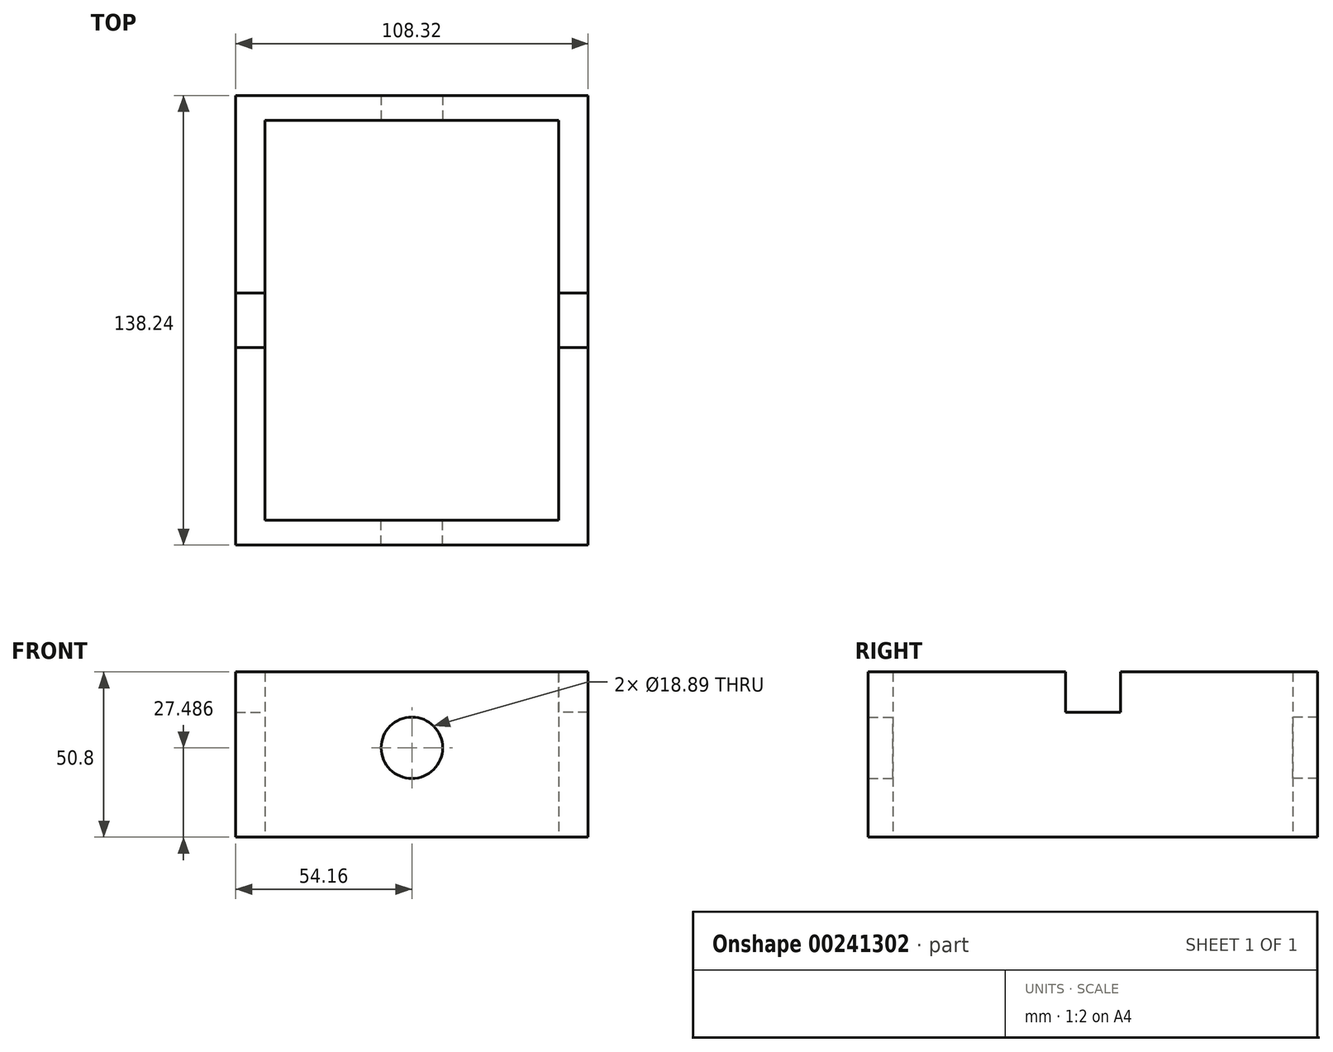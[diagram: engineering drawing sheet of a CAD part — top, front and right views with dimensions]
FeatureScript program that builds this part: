
annotation { "Feature Type Name" : "Feature", "Feature Type Description" : "" }
export const myFeature = defineFeature(function(context is Context, id is Id, definition is map)
    precondition{}
    {
        {
            var Q0;
            Q0=qCreatedBy(makeId("Top.planeOp"),FACE);
            var sketch = newSketch(context, id + "F0", { "sketchPlane" : qUnion([Q0])});
            skLineSegment(sketch, "E0.bottom", {"start": v(54.16, -69.12) * mm, "end": v(-54.16, -69.12) * mm});
            skLineSegment(sketch, "E0.top", {"start": v(54.16, 69.12) * mm, "end": v(-54.16, 69.12) * mm});
            skLineSegment(sketch, "E0.left", {"start": v(54.16, -69.12) * mm, "end": v(54.16, 69.12) * mm});
            skLineSegment(sketch, "E0.right", {"start": v(-54.16, -69.12) * mm, "end": v(-54.16, 69.12) * mm});
            skPoint(sketch, "E0.middle", {"position": v(0, 0) * mm});
            skSolve(sketch);
        }
        {
            var Q0;
            Q0=makeQuery(id+"F0.imprint","IMPRINT",FACE,{"disambiguationData":[TD([[makeQuery(id+"F0.imprint","IMPRINT",EDGE,{"derivedFrom":sQuery(id+"F0.wireOp",EDGE,"E0.bottom")}),-1.0]])]});
            extrude(context, id + "F1", {"entities" : qUnion([Q0]), "depth" : 50.8 * mm});
        }
        {
            var Q0;
            Q0=qCreatedBy(makeId("Top.planeOp"),FACE);
            var sketch = newSketch(context, id + "F2", { "sketchPlane" : qUnion([Q0])});
            skLineSegment(sketch, "E1.bottom", {"start": v(45.18, -61.5) * mm, "end": v(-45.18, -61.5) * mm});
            skLineSegment(sketch, "E1.top", {"start": v(45.18, 61.5) * mm, "end": v(-45.18, 61.5) * mm});
            skLineSegment(sketch, "E1.left", {"start": v(45.18, -61.5) * mm, "end": v(45.18, 61.5) * mm});
            skLineSegment(sketch, "E1.right", {"start": v(-45.18, -61.5) * mm, "end": v(-45.18, 61.5) * mm});
            skPoint(sketch, "E1.middle", {"position": v(0, 0) * mm});
            skSolve(sketch);
        }
        {
            var Q0;
            Q0=makeQuery(id+"F2.imprint","IMPRINT",FACE,{"disambiguationData":[TD([[makeQuery(id+"F2.imprint","IMPRINT",EDGE,{"derivedFrom":sQuery(id+"F2.wireOp",EDGE,"E1.bottom")}),-1.0]])]});
            extrude(context, id + "F3", {"entities" : qUnion([Q0]), "operationType" : NewBodyOperationType.REMOVE, "depth" : 111 * mm});
        }
        {
            var Q0;
            Q0=qCreatedBy(makeId("Right.planeOp"),FACE);
            var sketch = newSketch(context, id + "F4", { "sketchPlane" : qUnion([Q0])});
            skLineSegment(sketch, "E2.bottom", {"start": v(-8.44, 38.37) * mm, "end": v(8.44, 38.37) * mm});
            skLineSegment(sketch, "E2.top", {"start": v(-8.44, 50.9) * mm, "end": v(8.44, 50.9) * mm});
            skLineSegment(sketch, "E2.left", {"start": v(-8.44, 38.37) * mm, "end": v(-8.44, 50.9) * mm});
            skLineSegment(sketch, "E2.right", {"start": v(8.44, 38.37) * mm, "end": v(8.44, 50.9) * mm});
            skPoint(sketch, "E2.middle", {"position": v(0, 44.63) * mm});
            skSolve(sketch);
        }
        {
            var Q0;
            Q0=makeQuery(id+"F4.imprint","IMPRINT",FACE,{"disambiguationData":[TD([[makeQuery(id+"F4.imprint","IMPRINT",EDGE,{"derivedFrom":sQuery(id+"F4.wireOp",EDGE,"E2.bottom")}),1.0]])]});
            extrude(context, id + "F5", {"entities" : qUnion([Q0]), "operationType" : NewBodyOperationType.REMOVE, "oppositeDirection" : true, "depth" : 66.8 * mm});
        }
        {
            var Q0;
            Q0 = qSketchRegion(id + "F4", true);
            extrude(context, id + "F6", {"entities" : qUnion([Q0]), "operationType" : NewBodyOperationType.REMOVE, "depth" : 162.56 * mm});
        }
        {
            var Q0;
            Q0=qCreatedBy(makeId("Front.planeOp"),FACE);
            var sketch = newSketch(context, id + "F7", { "sketchPlane" : qUnion([Q0])});
            skCircle(sketch, "E3", {"center": v(0, 27.49) * mm, "radius": 9.45 * mm});
            skSolve(sketch);
        }
        {
            var Q0;
            Q0=makeQuery(id+"F7.imprint","IMPRINT",FACE,{"disambiguationData":[TD([[makeQuery(id+"F7.imprint","IMPRINT",EDGE,{"derivedFrom":sQuery(id+"F7.wireOp",EDGE,"E3")}),1.0]])]});
            extrude(context, id + "F8", {"entities" : qUnion([Q0]), "operationType" : NewBodyOperationType.REMOVE, "depth" : 123.95 * mm});
        }
        {
            var Q0;
            Q0 = qSketchRegion(id + "F7", true);
            extrude(context, id + "F9", {"entities" : qUnion([Q0]), "operationType" : NewBodyOperationType.REMOVE, "oppositeDirection" : true, "depth" : 117.6 * mm});
        }
    });
